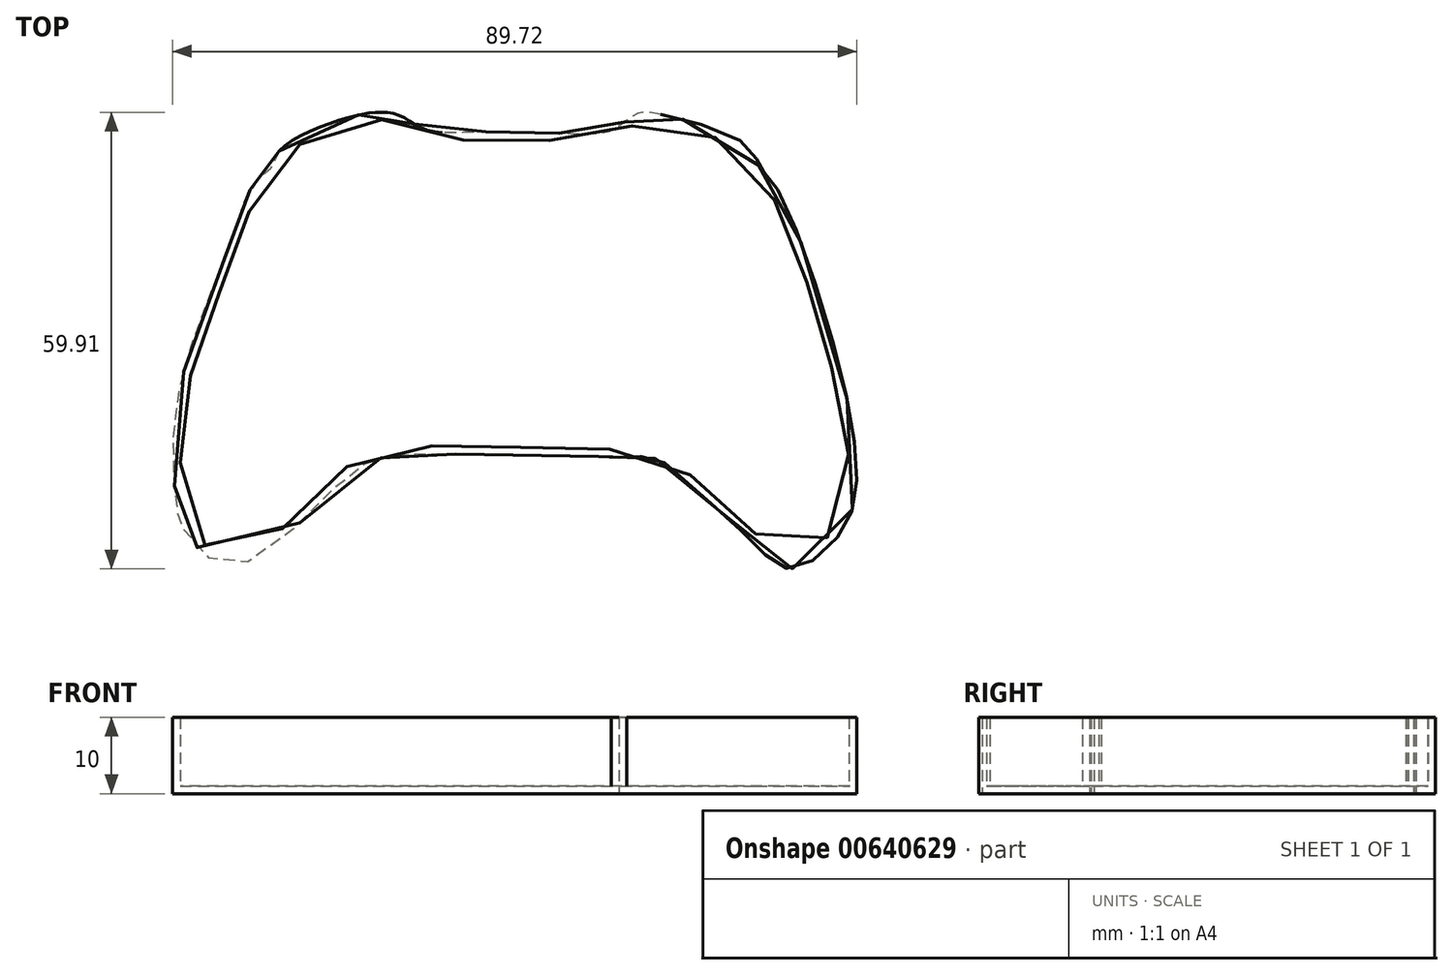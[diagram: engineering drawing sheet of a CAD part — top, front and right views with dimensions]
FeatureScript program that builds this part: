
annotation { "Feature Type Name" : "Feature", "Feature Type Description" : "" }
export const myFeature = defineFeature(function(context is Context, id is Id, definition is map)
    precondition{}
    {
        {
            var Q0;
            Q0=qCreatedBy(makeId("Top.planeOp"),FACE);
            var sketch = newSketch(context, id + "F0", { "sketchPlane" : qUnion([Q0])});
            skFitSpline(sketch, "E0", {"points": [v(-22.55, 42.97) * mm, v(-23.74, 40.59) * mm, v(-25.07, 39.55) * mm, v(-27.15, 36.28) * mm, v(-28.64, 31.68) * mm, v(-33.37, 19.55) * mm, v(-36.51, 4.94) * mm, v(-35.92, -4.42) * mm, v(-35.47, -6) * mm, v(-29.01, -11.41) * mm, v(-13.98, 0) * mm, v(-9.02, 2.72) * mm, v(-5.12, 3.17) * mm, v(7.25, 3.1) * mm, v(22.03, 2.72) * mm, v(21.99, 2.7) * mm, v(22.03, 2.72) * mm, v(26.3, 2.72) * mm, v(30.35, 0) * mm, v(39.22, -8) * mm, v(44.47, -11.86) * mm, v(50.94, -7.35) * mm, v(53.2, 0) * mm, v(49.72, 19.1) * mm, v(42.07, 39.08) * mm, v(40.44, 40.86) * mm, v(38.76, 43.74) * mm, v(26.44, 47.95) * mm, v(24.45, 47.86) * mm, v(22.78, 46.8) * mm, v(20.5, 45.43) * mm, v(13.8, 45.28) * mm, v(7.86, 45.43) * mm, v(2.83, 45.43) * mm, v(-3.26, 45.73) * mm, v(-6.6, 47.56) * mm, v(-9.8, 48.02) * mm, v(-14.83, 46.95) * mm, v(-22.55, 42.97) * mm]});
            skSolve(sketch);
        }
        {
            var Q0;
            Q0=makeQuery(id+"F0.imprint","IMPRINT",FACE,{"disambiguationData":[TD([[makeQuery(id+"F0.imprint","IMPRINT",EDGE,{"derivedFrom":sQuery(id+"F0.wireOp",EDGE,"E0")}),1.0]])]});
            extrude(context, id + "F1", {"entities" : qUnion([Q0]), "depth" : 10 * mm, "offsetDistance" : 25 * mm});
        }
        {
            var Q0;
            Q0=makeQuery(id+"F1.opExtrude","CAP_FACE",FACE,{"disambiguationData":[OSD([sQuery(id+"F0.wireOp",EDGE,"E0")])],"isStart":false});
            shell(context, id + "F2", {"entities" : qUnion([Q0]), "thickness" : 1 * mm});
        }
    });
